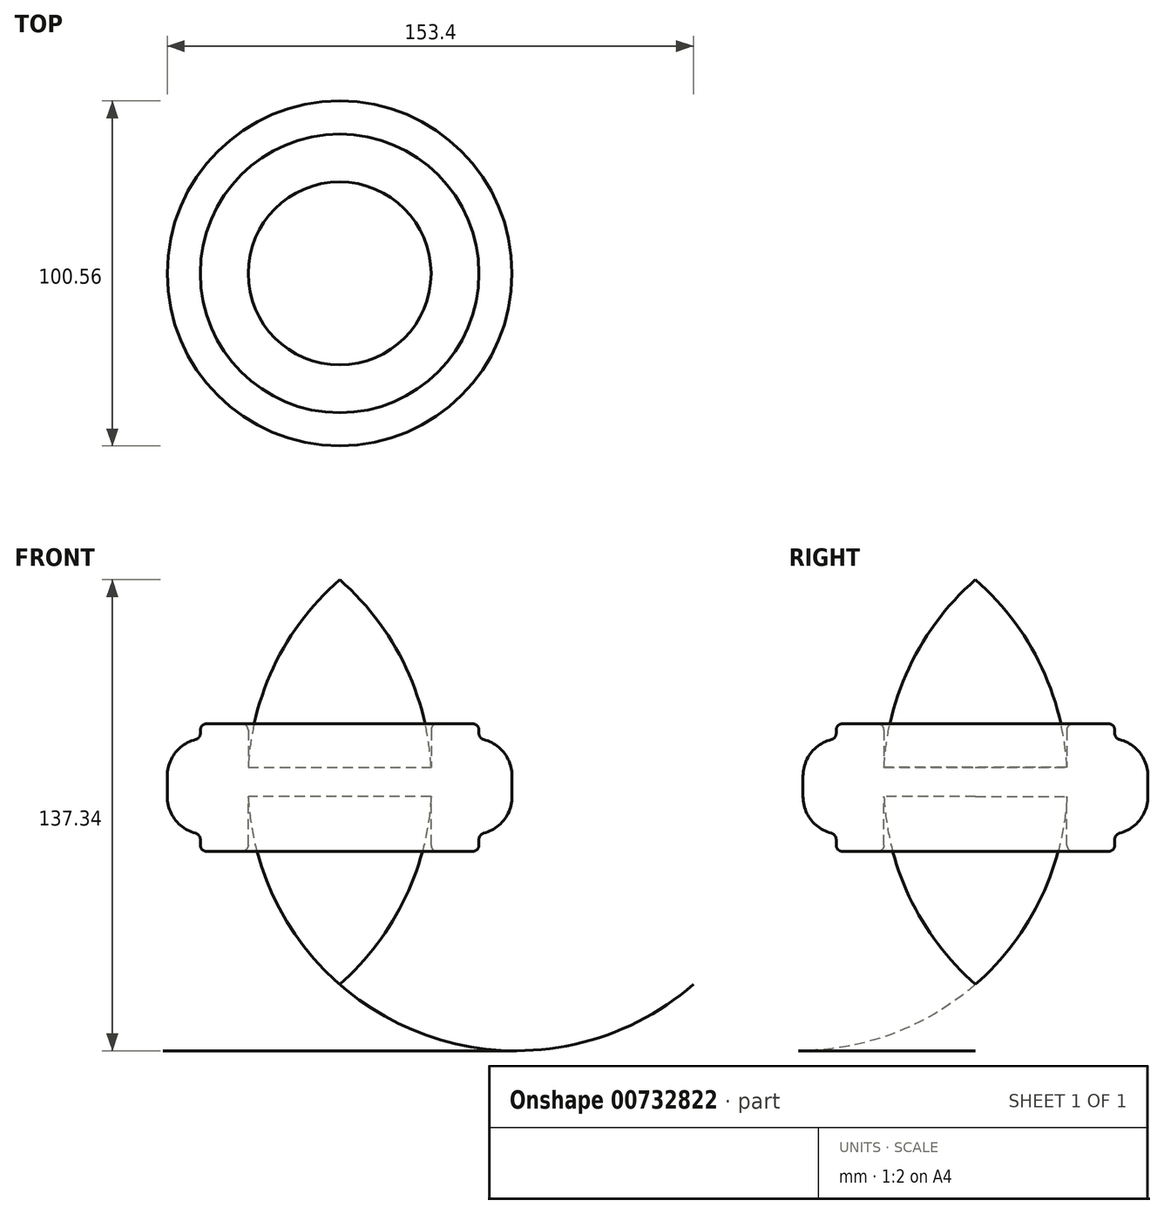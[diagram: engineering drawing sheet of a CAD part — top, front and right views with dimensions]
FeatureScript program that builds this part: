
annotation { "Feature Type Name" : "Feature", "Feature Type Description" : "" }
export const myFeature = defineFeature(function(context is Context, id is Id, definition is map)
    precondition{}
    {
        {
            var Q0;
            Q0=qCreatedBy(makeId("Front.planeOp"),FACE);
            var sketch = newSketch(context, id + "F0", { "sketchPlane" : qUnion([Q0])});
            skArc(sketch, "E0", {"start": v(0, -56.88) * mm, "mid": v(26.79, 2.1) * mm, "end": v(0, 61.1) * mm});
            skLineSegment(sketch, "E1.bottom", {"start": v(40.62, 14.76) * mm, "end": v(50.28, 14.76) * mm});
            skLineSegment(sketch, "E1.top", {"start": v(40.62, -13.1) * mm, "end": v(50.28, -13.1) * mm});
            skLineSegment(sketch, "E1.left", {"start": v(40.62, 14.76) * mm, "end": v(40.62, -13.1) * mm});
            skLineSegment(sketch, "E1.right", {"start": v(50.28, 14.76) * mm, "end": v(50.28, -13.1) * mm});
            skLineSegment(sketch, "E2", {"start": v(0, 61.1) * mm, "end": v(0, -56.88) * mm});
            skLineSegment(sketch, "E3", {"start": v(0, 81) * mm, "end": v(0, -75.93) * mm, "construction": true});
            skLineSegment(sketch, "E4.bottom", {"start": v(26.67, 6.37) * mm, "end": v(40.62, 6.37) * mm});
            skLineSegment(sketch, "E4.top", {"start": v(26.67, -5.42) * mm, "end": v(40.62, -5.42) * mm});
            skLineSegment(sketch, "E4.left", {"start": v(26.67, 6.37) * mm, "end": v(26.67, -5.42) * mm});
            skLineSegment(sketch, "E4.right", {"start": v(40.62, 6.37) * mm, "end": v(40.62, -5.42) * mm});
            skSolve(sketch);
        }
        {
            var Q0;
            Q0 = qSketchRegion(id + "F0", true);
            var Q1;
            Q1=sQuery(id+"F0.wireOp",EDGE,"E3");
            revolve(context, id + "F1", {"surfaceOperationType" : NewSurfaceOperationType.NEW, "entities" : qUnion([Q0]), "axis" : qUnion([Q1]), "revolveType" : RevolveType.FULL});
        }
        {
            var Q0;
            Q0=makeQuery(id+"F1.opRevolve","SWEPT_FACE",FACE,{"disambiguationData":[OSD([sQuery(id+"F0.wireOp",EDGE,"E4.bottom")])]});
            var Q1;
            Q1=makeQuery(id+"F1.opRevolve","SWEPT_FACE",FACE,{"disambiguationData":[OSD([sQuery(id+"F0.wireOp",EDGE,"E4.top")])]});
            extrude(context, id + "F2", {"entities" : qUnion([Q0, Q1]), "operationType" : NewBodyOperationType.ADD, "endBound" : BoundingType.SYMMETRIC, "depth" : 25.4 * mm, "offsetDistance" : 25.4 * mm});
        }
        {
            var Q0;
            Q0=makeQuery(id+"F1.opRevolve","SWEPT_EDGE",EDGE,{"disambiguationData":[OSD([sQuery(id+"F0.wireOp",EDGE,"E1.bottom"),sQuery(id+"F0.wireOp",EDGE,"E1.right")])]});
            var Q1;
            Q1=makeQuery(id+"F1.opRevolve","SWEPT_EDGE",EDGE,{"disambiguationData":[OSD([sQuery(id+"F0.wireOp",EDGE,"E1.top"),sQuery(id+"F0.wireOp",EDGE,"E1.right")])]});
            fillet(context, id + "F3", {"entities" : qUnion([Q0, Q1]), "radius" : 11.04 * mm, "tangentPropagation" : true, "allowEdgeOverflow" : false});
        }
        {
            var Q0;
            Q0=makeQuery(id+"F2.opExtrude","CAP_EDGE",EDGE,{"disambiguationData":[OSD([sQuery(id+"F0.wireOp",EDGE,"E1.left"),sQuery(id+"F0.wireOp",EDGE,"E4.bottom"),sQuery(id+"F0.wireOp",EDGE,"E4.right")])],"isStart":false});
            var Q1;
            Q1=makeQuery(id+"F2.opExtrude","CAP_EDGE",EDGE,{"disambiguationData":[OSD([sQuery(id+"F0.wireOp",EDGE,"E0"),sQuery(id+"F0.wireOp",EDGE,"E4.bottom"),sQuery(id+"F0.wireOp",EDGE,"E4.left")])],"isStart":false});
            var Q2;
            {var subQ0=sQuery(id+"F0.wireOp",EDGE,"E4.right");var subQ1=sQuery(id+"F0.wireOp",EDGE,"E1.left");Q2=makeQuery(id+"F3.opFillet","BLEND_EDGE",EDGE,{"blendedFrom":[makeQuery(id+"F1.opRevolve","SWEPT_EDGE",EDGE,{"disambiguationData":[OSD([sQuery(id+"F0.wireOp",EDGE,"E1.bottom"),sQuery(id+"F0.wireOp",EDGE,"E1.right")])]}),makeQuery(id+"F2.boolean.opBoolean","MERGE",FACE,{"disambiguationData":[OD(0.0)],"derivedFrom":[makeQuery(id+"F2.opExtrude","SWEPT_FACE",FACE,{"disambiguationData":[OSD([subQ1,sQuery(id+"F0.wireOp",EDGE,"E4.bottom"),subQ0])]}),makeQuery(id+"F2.opExtrude","SWEPT_FACE",FACE,{"disambiguationData":[OSD([subQ1,sQuery(id+"F0.wireOp",EDGE,"E4.top"),subQ0])]})]})],"blendedInto":[makeQuery(id+"F2.boolean.opBoolean","MERGE",FACE,{"disambiguationData":[OD(0.0)],"derivedFrom":[makeQuery(id+"F2.opExtrude","SWEPT_FACE",FACE,{"disambiguationData":[OSD([subQ1,sQuery(id+"F0.wireOp",EDGE,"E4.bottom"),subQ0])]}),makeQuery(id+"F2.opExtrude","SWEPT_FACE",FACE,{"disambiguationData":[OSD([subQ1,sQuery(id+"F0.wireOp",EDGE,"E4.top"),subQ0])]})]})]});}
            var Q3;
            Q3=makeQuery(id+"F2.opExtrude","CAP_EDGE",EDGE,{"disambiguationData":[OSD([sQuery(id+"F0.wireOp",EDGE,"E1.left"),sQuery(id+"F0.wireOp",EDGE,"E4.top"),sQuery(id+"F0.wireOp",EDGE,"E4.right")])],"isStart":true});
            var Q4;
            {var subQ0=sQuery(id+"F0.wireOp",EDGE,"E4.right");var subQ1=sQuery(id+"F0.wireOp",EDGE,"E1.left");Q4=makeQuery(id+"F3.opFillet","BLEND_EDGE",EDGE,{"blendedFrom":[makeQuery(id+"F1.opRevolve","SWEPT_EDGE",EDGE,{"disambiguationData":[OSD([sQuery(id+"F0.wireOp",EDGE,"E1.top"),sQuery(id+"F0.wireOp",EDGE,"E1.right")])]}),makeQuery(id+"F2.boolean.opBoolean","MERGE",FACE,{"disambiguationData":[OD(1.0)],"derivedFrom":[makeQuery(id+"F2.opExtrude","SWEPT_FACE",FACE,{"disambiguationData":[OSD([subQ1,sQuery(id+"F0.wireOp",EDGE,"E4.bottom"),subQ0])]}),makeQuery(id+"F2.opExtrude","SWEPT_FACE",FACE,{"disambiguationData":[OSD([subQ1,sQuery(id+"F0.wireOp",EDGE,"E4.top"),subQ0])]})]})],"blendedInto":[makeQuery(id+"F2.boolean.opBoolean","MERGE",FACE,{"disambiguationData":[OD(1.0)],"derivedFrom":[makeQuery(id+"F2.opExtrude","SWEPT_FACE",FACE,{"disambiguationData":[OSD([subQ1,sQuery(id+"F0.wireOp",EDGE,"E4.bottom"),subQ0])]}),makeQuery(id+"F2.opExtrude","SWEPT_FACE",FACE,{"disambiguationData":[OSD([subQ1,sQuery(id+"F0.wireOp",EDGE,"E4.top"),subQ0])]})]})]});}
            var Q5;
            Q5=makeQuery(id+"F2.opExtrude","CAP_EDGE",EDGE,{"disambiguationData":[OSD([sQuery(id+"F0.wireOp",EDGE,"E4.top"),sQuery(id+"F0.wireOp",EDGE,"E4.left")])],"isStart":true});
            fillet(context, id + "F4", {"entities" : qUnion([Q0, Q1, Q2, Q3, Q4, Q5]), "radius" : 1.83 * mm, "tangentPropagation" : true, "allowEdgeOverflow" : false});
        }
    });
